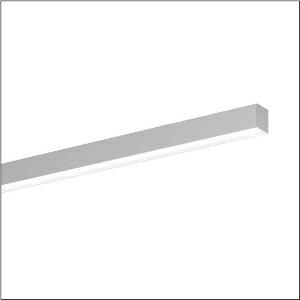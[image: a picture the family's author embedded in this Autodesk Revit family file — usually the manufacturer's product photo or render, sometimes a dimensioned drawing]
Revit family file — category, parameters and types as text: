
# Revit family: silica_r__21_51mx23dc3asb_5b95
name_source: partatom
category: Lighting Fixtures
units: mm (PartAtom-declared; Revit-internal decimal feet)

## family parameters
Cut with Voids When Loaded = No
Host = Face
Light Source = No
Part Type = Normal
Room Calculation Point = No
Round Connector Dimension = Use Diameter
Shared = No

## types (1)
- --- (1 x LED, 8200 lm, 62.2 W, 3000K)
    Apparent Load = 62 VA
    CIE Flux Codes = 78 96 99 100 100
    Color Rendering = 80
    Color Temperature = 3000K
    Default Elevation = 1800 mm
    Description = Silica® 21, office luminaire, primary optical cover: prismatic diffuser, of PMMA, CAT 2 (L<= 3000cd/m²), light emission: direct distribution, primary light characteristic: symmetric, installation type: surface-mounted, LED, rated luminous flux: 8.200lm, luminous efficacy: 132lm/W, light colour: 830, colour temperature: 3000K, with terminal, 3+2-pole, max. 2.5mm², mains connection: 220..240V, AC, 50/60Hz, rated input power: 62.2W, luminaire housing, of aluminium, metallic grey (RAL 9006), length: 3.004mm, width: 53mm, height: 53mm, protection rating (complete): IP20, insulation class (complete): insulation class I (protective earthing), certification: CE, permissible operating ambient temperature: 0..+35°C, standard: EN 50419, packaging unit: 1 piece
    Height = 0 mm  [stored 0 ft]
    Lamp = 1 x LED
    Lamp Light Flux = 8200 lm
    Lamp Power = 62.2 W
    Lamp count = 1
    Length = 3004 mm
    Luminous efficacy = 132 lm/W
    Manufacturer = Siteco
    ModVariant = No
    Model = 51MX23DC3ASB
    Mounting Place = Ceiling
    Mounting Type = Recessed
    Number of Poles = 1
    OnlyDefault = Yes
    Power Factor = 1
    Product Name = Silica® 21
    Product group = office luminaire | ceiling recessed
    ProductGroupID = 401
    Protection Class = Protection class I
    Protection Degree = IP 20
    RLX_Detail_Level = 1
    RLX_Emergency_Light_Flux = 0 lm
    RLX_Emergency_Type = 0
    RLX_Emergency_Type_DB = No
    RlxData = <blob elided: 21221 chars, md5=77a4e2e2>
    Socket = socket
    Standby Power = 0 W
    System Light Flux = 8200 lm
    System Power = 62 W
    Type Comments = factory setting: luminous flux: 100 % | dim-lin: 254 | 345 mA
    Type Image = l_1297768.jpg
    URL = http://relux.com
    VarID = @adj_049571
    Voltage = 0 V
    Weight = 0.00 kg
    Width = 53 mm

note: [stored X ft] marks values corroborated as IEEE doubles in the binary element streams (Revit-internal decimal feet)

## geometry (parser evidence)
native form markers: Blend x4, Sweep x10
no freeform markers — native parametric forms only
